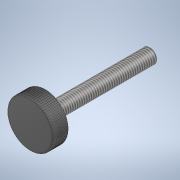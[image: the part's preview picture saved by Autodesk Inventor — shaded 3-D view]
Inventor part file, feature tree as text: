
AUTODESK INVENTOR PART (.ipt)
format: ipt  version: 2020 (Build 240168000, 168)  size: 619,520 bytes
history: native  units: mm
features: projected_geometry x5, extrude x4, sketch x4, fillet x2, chamfer x1, thread x1, pattern_circular x1
ambient origin geometry x8: Origin, YZ Plane, XZ Plane, XY Plane, X Axis, Y Axis, Z Axis, Center Point
bodies: Solid1 (feature_tree)
feature tree (18):
  extrude  "Extrusion1"  Depth=6.5mm TaperAngle=0.0deg
  extrude  "Extrusion2"  Depth=35.0mm TaperAngle=0.0deg
  extrude  "Extrusion3"  Depth=1.0mm TaperAngle=0.0deg
  chamfer  "Chamfer1"  Distance=0.25mm Angle=45.0deg
  fillet  "Fillet1"  Radius=0.5mm
  fillet  "Fillet2"  Radius=0.25mm
  thread  "Thread1"  [1 undecoded]
  extrude  "Extrusion4"  Depth=0.375mm
  pattern_circular  "Circular Pattern1"  [2 undecoded]
  sketch  "Sketch1"  dims[d0=16.0mm d1=6.5mm d2=0.0mm]
  sketch  "Sketch2"  dims[d3=5.0mm d4=35.0mm d5=0.0mm]
  sketch  "Sketch3"  dims[d7=12.0mm d8=1.0mm d9=0.0mm d10=0.25mm d11=2.0mm d12=45.0deg d13=0.5mm d14=0.25mm d15=19.75mm d16=0.0mm]
  sketch  "Sketch4"  dims[d17=0.375mm d18=0.25mm d19=0.0mm d20=0.0mm d21=750.0mm d22=360.0deg]
  projected_geometry  "Project Cut Edges1"
  projected_geometry  "Project Cut Edges2"
  projected_geometry  "Project Cut Edges3"
  projected_geometry  "Project Cut Edges4"
  projected_geometry  "Project Cut Edges5"
note: 3 required parameter values undecoded (feature->parameter linkage not recoverable at this tier; creation-order binding heuristic only, values carry confidence <= 0.55)
